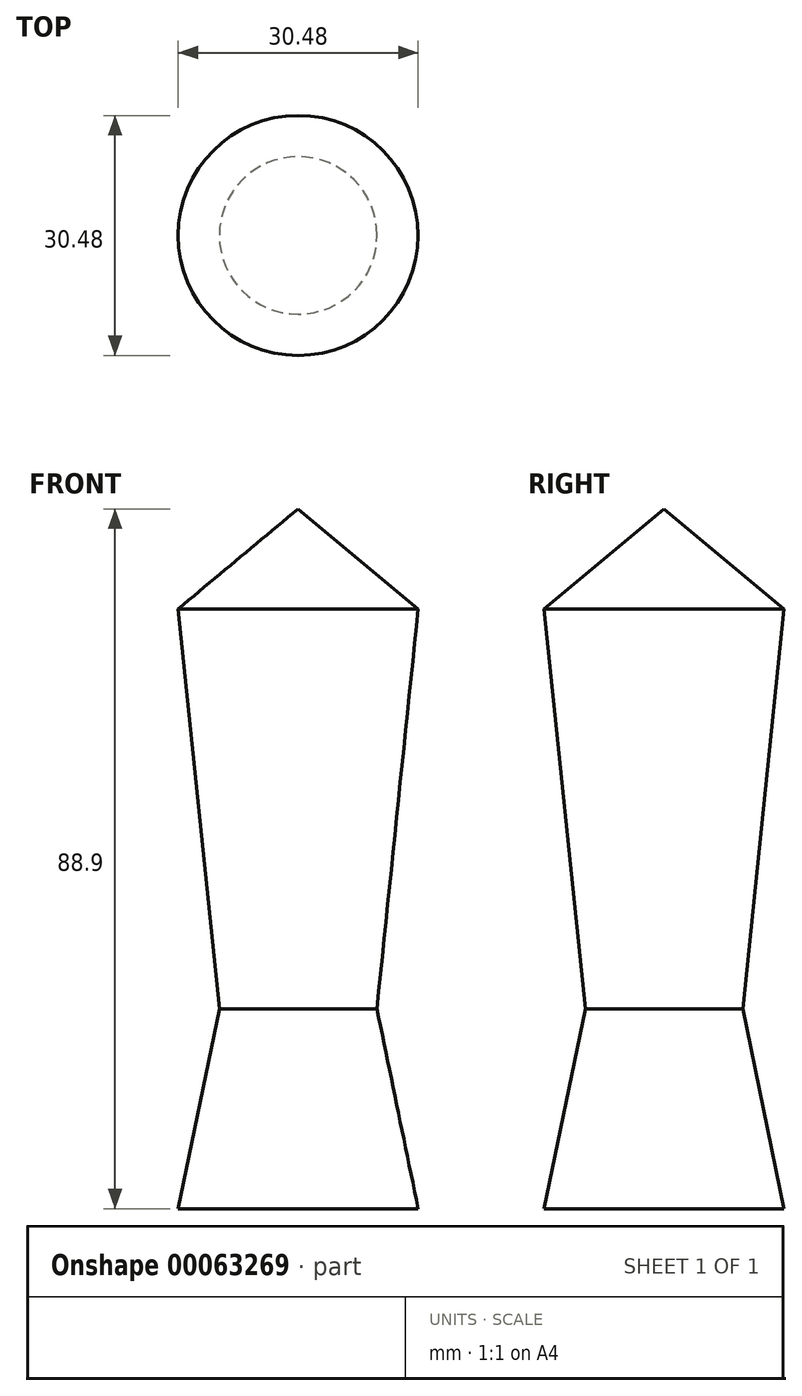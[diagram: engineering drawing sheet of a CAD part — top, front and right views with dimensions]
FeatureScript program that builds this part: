
annotation { "Feature Type Name" : "Feature", "Feature Type Description" : "" }
export const myFeature = defineFeature(function(context is Context, id is Id, definition is map)
    precondition{}
    {
        {
            var Q0;
            Q0=qCreatedBy(makeId("Front.planeOp"),FACE);
            var sketch = newSketch(context, id + "F0", { "sketchPlane" : qUnion([Q0])});
            skLineSegment(sketch, "E0", {"start": v(0, 0) * mm, "end": v(-15.24, 0) * mm});
            skLineSegment(sketch, "E1", {"start": v(-15.24, 0) * mm, "end": v(-10, 25.4) * mm});
            skLineSegment(sketch, "E2", {"start": v(-10, 25.4) * mm, "end": v(0, 25.4) * mm});
            skLineSegment(sketch, "E3", {"start": v(0, 25.4) * mm, "end": v(0, 0) * mm});
            skSolve(sketch);
        }
        {
            var Q0;
            Q0=makeQuery(id+"F0.imprint","IMPRINT",FACE,{"disambiguationData":[TD([[makeQuery(id+"F0.imprint","IMPRINT",EDGE,{"derivedFrom":sQuery(id+"F0.wireOp",EDGE,"E0")}),-1.0]])]});
            var Q1;
            Q1=sQuery(id+"F0.wireOp",EDGE,"E3");
            revolve(context, id + "F1", {"entities" : qUnion([Q0]), "axis" : qUnion([Q1]), "revolveType" : RevolveType.FULL});
        }
        {
            var Q0;
            Q0=qCreatedBy(makeId("Front.planeOp"),FACE);
            var sketch = newSketch(context, id + "F2", { "sketchPlane" : qUnion([Q0])});
            skLineSegment(sketch, "E4.0", {"start": v(-10, 25.4) * mm, "end": v(10, 25.4) * mm});
            skLineSegment(sketch, "E5", {"start": v(0, 25.4) * mm, "end": v(0, 76.2) * mm});
            skLineSegment(sketch, "E6", {"start": v(0, 76.2) * mm, "end": v(-15.24, 76.2) * mm});
            skLineSegment(sketch, "E7", {"start": v(-15.24, 76.2) * mm, "end": v(-10, 25.4) * mm});
            skSolve(sketch);
        }
        {
            var Q0;
            Q0 = qSketchRegion(id + "F2", true);
            var Q1;
            Q1=sQuery(id+"F2.wireOp",EDGE,"E5");
            revolve(context, id + "F3", {"operationType" : NewBodyOperationType.ADD, "entities" : qUnion([Q0]), "axis" : qUnion([Q1]), "revolveType" : RevolveType.FULL});
        }
        {
            var Q0;
            Q0=qCreatedBy(makeId("Front.planeOp"),FACE);
            var sketch = newSketch(context, id + "F4", { "sketchPlane" : qUnion([Q0])});
            skLineSegment(sketch, "E8.0", {"start": v(15.24, 76.2) * mm, "end": v(-15.24, 76.2) * mm});
            skLineSegment(sketch, "E9", {"start": v(0, 76.2) * mm, "end": v(0, 88.9) * mm});
            skPoint(sketch, "E9.endSnap0", {"position": v(0, 76.2) * mm});
            skLineSegment(sketch, "E10", {"start": v(0, 88.9) * mm, "end": v(-15.24, 76.2) * mm});
            skSolve(sketch);
        }
        {
            var Q0;
            {var subQ2=sQuery(id+"F4.wireOp",EDGE,"E9");Q0=makeQuery(id+"F4.imprint","IMPRINT",FACE,{"disambiguationData":[TD([[makeQuery(id+"F4.imprint","IMPRINT",EDGE,{"derivedFrom":subQ2}),1.0]])]});}
            var Q1;
            Q1=sQuery(id+"F4.wireOp",EDGE,"E9");
            revolve(context, id + "F5", {"operationType" : NewBodyOperationType.ADD, "entities" : qUnion([Q0]), "axis" : qUnion([Q1]), "revolveType" : RevolveType.FULL});
        }
    });
